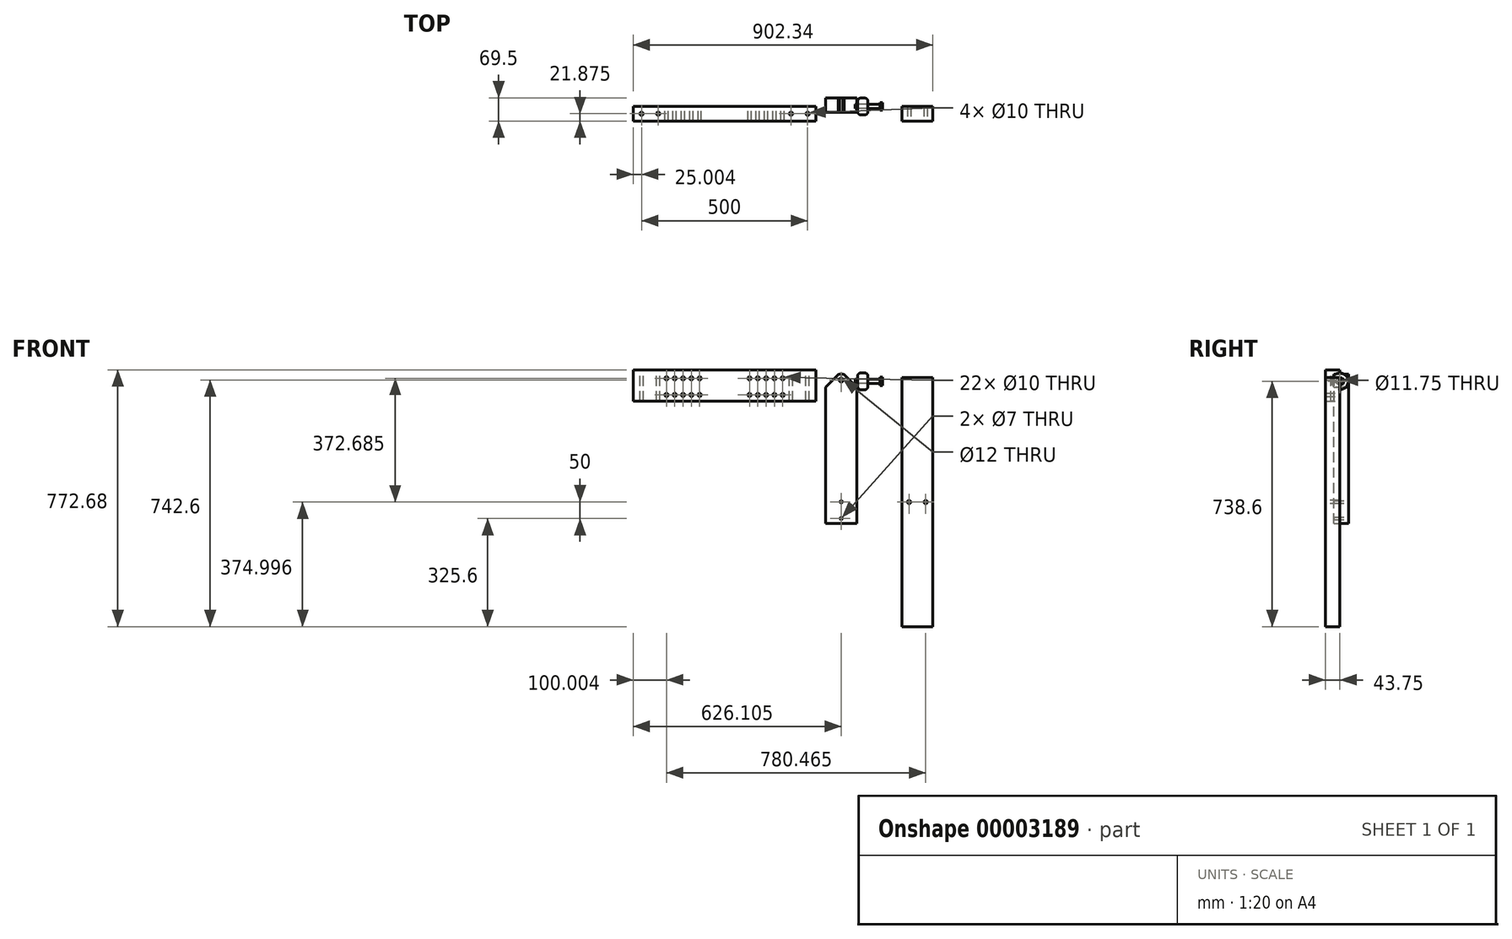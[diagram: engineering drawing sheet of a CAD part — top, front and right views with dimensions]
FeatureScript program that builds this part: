
annotation { "Feature Type Name" : "Feature", "Feature Type Description" : "" }
export const myFeature = defineFeature(function(context is Context, id is Id, definition is map)
    precondition{}
    {
        {
            var Q0;
            Q0=qCreatedBy(makeId("Top.planeOp"),FACE);
            var sketch = newSketch(context, id + "F0", { "sketchPlane" : qUnion([Q0])});
            skLineSegment(sketch, "E0.top", {"start": v(-30, 5.88) * mm, "end": v(0, 5.88) * mm});
            skLineSegment(sketch, "E0.left", {"start": v(-30, 17) * mm, "end": v(-30, 5.88) * mm});
            skLineSegment(sketch, "E0.right", {"start": v(0, 17) * mm, "end": v(0, 5.88) * mm});
            skLineSegment(sketch, "E1", {"start": v(0, 0) * mm, "end": v(-31.96, 0) * mm, "construction": true});
            skLineSegment(sketch, "E2", {"start": v(-22, 25) * mm, "end": v(-8, 25) * mm});
            skPoint(sketch, "E3.visualSharp", {"position": v(-30, 25) * mm});
            skArc(sketch, "E3.filletArc", {"start": v(-22, 25) * mm, "mid": v(-27.66, 22.66) * mm, "end": v(-30, 17) * mm});
            skPoint(sketch, "E4.visualSharp", {"position": v(0, 25) * mm});
            skArc(sketch, "E4.filletArc", {"start": v(0, 17) * mm, "mid": v(-2.34, 22.66) * mm, "end": v(-8, 25) * mm});
            skSolve(sketch);
        }
        {
            var Q0;
            Q0 = qSketchRegion(id + "F0", true);
            var Q1;
            Q1=sQuery(id+"F0.wireOp",EDGE,"E1");
            revolve(context, id + "F1", {"entities" : qUnion([Q0]), "axis" : qUnion([Q1]), "revolveType" : RevolveType.FULL});
        }
        {
            var Q0;
            Q0=qCreatedBy(makeId("Right.planeOp"),FACE);
            var sketch = newSketch(context, id + "F2", { "sketchPlane" : qUnion([Q0])});
            skCircle(sketch, "E5.0", {"center": v(0, 0) * mm, "radius": 5.88 * mm});
            skSolve(sketch);
        }
        {
            var Q0;
            Q0=makeQuery(id+"F2.imprint","IMPRINT",FACE,{"disambiguationData":[TD([[makeQuery(id+"F2.imprint","IMPRINT",EDGE,{"derivedFrom":sQuery(id+"F2.wireOp",EDGE,"E5.0")}),1.0]])]});
            extrude(context, id + "F3", {"entities" : qUnion([Q0]), "endBound" : BoundingType.SYMMETRIC, "depth" : (3 * 25) * mm});
        }
        {
            var Q0;
            Q0=makeQuery(id+"F3.opExtrude","CAP_FACE",FACE,{"disambiguationData":[OSD([sQuery(id+"F2.wireOp",EDGE,"E5.0")])],"isStart":false});
            var sketch = newSketch(context, id + "F4", { "sketchPlane" : qUnion([Q0])});
            skCircle(sketch, "E6.cCircle", {"center": v(0, 0) * mm, "radius": 10.81 * mm, "construction": true});
            skLineSegment(sketch, "E6.0", {"start": v(11.76, 4.21) * mm, "end": v(9.52, -8.08) * mm});
            skLineSegment(sketch, "E6.1", {"start": v(9.52, -8.08) * mm, "end": v(-2.23, -12.29) * mm});
            skLineSegment(sketch, "E6.2", {"start": v(-2.23, -12.29) * mm, "end": v(-11.76, -4.21) * mm});
            skLineSegment(sketch, "E6.3", {"start": v(-11.76, -4.21) * mm, "end": v(-9.52, 8.08) * mm});
            skLineSegment(sketch, "E6.4", {"start": v(-9.52, 8.08) * mm, "end": v(2.23, 12.29) * mm});
            skLineSegment(sketch, "E6.5", {"start": v(2.23, 12.29) * mm, "end": v(11.76, 4.21) * mm});
            skPoint(sketch, "E6.0.midPoint", {"position": v(10.64, -1.93) * mm});
            skSolve(sketch);
        }
        {
            var Q0;
            Q0=makeQuery(id+"F4.imprint","IMPRINT",FACE,{"disambiguationData":[TD([[makeQuery(id+"F4.imprint","IMPRINT",EDGE,{"derivedFrom":sQuery(id+"F4.wireOp",EDGE,"E6.0")}),-1.0]])]});
            var Q1;
            Q1=makeQuery(id+"F4.imprint","IMPRINT",FACE,{"disambiguationData":[TD([[makeQuery(id+"F4.imprint","IMPRINT",EDGE,{"derivedFrom":makeQuery(id+"F3.opExtrude","CAP_EDGE",EDGE,{"disambiguationData":[OSD([sQuery(id+"F2.wireOp",EDGE,"E5.0")])],"isStart":false})}),1.0]])]});
            extrude(context, id + "F5", {"entities" : qUnion([Q0, Q1]), "operationType" : NewBodyOperationType.ADD, "depth" : 7.7 * mm});
        }
        {
            var Q0;
            Q0=qCreatedBy(makeId("Front.planeOp"),FACE);
            var sketch = newSketch(context, id + "F6", { "sketchPlane" : qUnion([Q0])});
            skLineSegment(sketch, "E7.bottom", {"start": v(-155.98, 34.08) * mm, "end": v(-705.98, 34.08) * mm});
            skLineSegment(sketch, "E7.top", {"start": v(-155.98, -59.67) * mm, "end": v(-705.98, -59.67) * mm});
            skLineSegment(sketch, "E7.left", {"start": v(-155.98, 34.08) * mm, "end": v(-155.98, -59.67) * mm});
            skLineSegment(sketch, "E7.right", {"start": v(-705.98, 34.08) * mm, "end": v(-705.98, -59.67) * mm});
            skLineSegment(sketch, "E8", {"start": v(-430.98, 34.08) * mm, "end": v(-430.98, -337.68) * mm, "construction": true});
            skCircle(sketch, "E9", {"center": v(-605.98, 9.08) * mm, "radius": 5 * mm});
            skCircle(sketch, "E10", {"center": v(-580.98, 9.08) * mm, "radius": 5 * mm});
            skCircle(sketch, "E11", {"center": v(-555.98, 9.08) * mm, "radius": 5 * mm});
            skCircle(sketch, "E12", {"center": v(-530.98, 9.08) * mm, "radius": 5 * mm});
            skCircle(sketch, "E13", {"center": v(-505.98, 9.08) * mm, "radius": 5 * mm});
            skCircle(sketch, "E14", {"center": v(-605.98, -40.92) * mm, "radius": 5 * mm});
            skCircle(sketch, "E15", {"center": v(-580.98, -40.92) * mm, "radius": 5 * mm});
            skCircle(sketch, "E16", {"center": v(-555.98, -40.92) * mm, "radius": 5 * mm});
            skCircle(sketch, "E17", {"center": v(-530.98, -40.92) * mm, "radius": 5 * mm});
            skCircle(sketch, "E18", {"center": v(-505.98, -40.92) * mm, "radius": 5 * mm});
            skLineSegment(sketch, "E19", {"start": v(-605.98, 9.08) * mm, "end": v(-580.98, 9.08) * mm, "construction": true});
            skLineSegment(sketch, "E20", {"start": v(-555.98, 9.08) * mm, "end": v(-580.98, 9.08) * mm, "construction": true});
            skLineSegment(sketch, "E21", {"start": v(-555.98, 9.08) * mm, "end": v(-530.98, 9.08) * mm, "construction": true});
            skLineSegment(sketch, "E22", {"start": v(-530.98, 9.08) * mm, "end": v(-505.98, 9.08) * mm, "construction": true});
            skLineSegment(sketch, "E23", {"start": v(-505.98, -40.92) * mm, "end": v(-530.98, -40.92) * mm, "construction": true});
            skLineSegment(sketch, "E24", {"start": v(-555.98, -40.92) * mm, "end": v(-530.98, -40.92) * mm, "construction": true});
            skLineSegment(sketch, "E25", {"start": v(-555.98, -40.92) * mm, "end": v(-580.98, -40.92) * mm, "construction": true});
            skLineSegment(sketch, "E26", {"start": v(-580.98, -40.92) * mm, "end": v(-605.98, -40.92) * mm, "construction": true});
            skLineSegment(sketch, "E27", {"start": v(-605.98, 9.08) * mm, "end": v(-605.98, -40.92) * mm, "construction": true});
            skLineSegment(sketch, "E28.0.MirrorCS", {"start": v(-305.98, 9.08) * mm, "end": v(-330.98, 9.08) * mm, "construction": true});
            skLineSegment(sketch, "E28.1.MirrorCS", {"start": v(-305.98, -40.92) * mm, "end": v(-330.98, -40.92) * mm, "construction": true});
            skLineSegment(sketch, "E28.2.MirrorCS", {"start": v(-255.98, 9.08) * mm, "end": v(-255.98, -40.92) * mm, "construction": true});
            skCircle(sketch, "E28.3.MirrorC", {"center": v(-255.98, -40.92) * mm, "radius": 5 * mm});
            skCircle(sketch, "E28.4.MirrorC", {"center": v(-305.98, 9.08) * mm, "radius": 5 * mm});
            skCircle(sketch, "E28.5.MirrorC", {"center": v(-255.98, 9.08) * mm, "radius": 5 * mm});
            skLineSegment(sketch, "E28.6.MirrorCS", {"start": v(-280.98, -40.92) * mm, "end": v(-255.98, -40.92) * mm, "construction": true});
            skLineSegment(sketch, "E28.7.MirrorCS", {"start": v(-255.98, 9.08) * mm, "end": v(-280.98, 9.08) * mm, "construction": true});
            skCircle(sketch, "E28.8.MirrorC", {"center": v(-330.98, -40.92) * mm, "radius": 5 * mm});
            skLineSegment(sketch, "E28.9.MirrorCS", {"start": v(-305.98, -40.92) * mm, "end": v(-280.98, -40.92) * mm, "construction": true});
            skLineSegment(sketch, "E28.10.MirrorCS", {"start": v(-305.98, 9.08) * mm, "end": v(-280.98, 9.08) * mm, "construction": true});
            skCircle(sketch, "E28.11.MirrorC", {"center": v(-330.98, 9.08) * mm, "radius": 5 * mm});
            skLineSegment(sketch, "E28.12.MirrorCS", {"start": v(-355.98, -40.92) * mm, "end": v(-330.98, -40.92) * mm, "construction": true});
            skCircle(sketch, "E28.13.MirrorC", {"center": v(-355.98, 9.08) * mm, "radius": 5 * mm});
            skCircle(sketch, "E28.14.MirrorC", {"center": v(-280.98, -40.92) * mm, "radius": 5 * mm});
            skLineSegment(sketch, "E28.15.MirrorCS", {"start": v(-330.98, 9.08) * mm, "end": v(-355.98, 9.08) * mm, "construction": true});
            skCircle(sketch, "E28.16.MirrorC", {"center": v(-280.98, 9.08) * mm, "radius": 5 * mm});
            skCircle(sketch, "E28.17.MirrorC", {"center": v(-355.98, -40.92) * mm, "radius": 5 * mm});
            skCircle(sketch, "E28.18.MirrorC", {"center": v(-305.98, -40.92) * mm, "radius": 5 * mm});
            skSolve(sketch);
        }
        {
            var Q0;
            Q0=makeQuery(id+"F6.imprint","IMPRINT",FACE,{"disambiguationData":[TD([[makeQuery(id+"F6.imprint","IMPRINT",EDGE,{"derivedFrom":sQuery(id+"F6.wireOp",EDGE,"E7.bottom")}),1.0]])]});
            extrude(context, id + "F7", {"entities" : qUnion([Q0]), "depth" : (1.75 * 25) * mm});
        }
        {
            var Q0;
            Q0=makeQuery(id+"F7.opExtrude","SWEPT_FACE",FACE,{"disambiguationData":[OSD([sQuery(id+"F6.wireOp",EDGE,"E7.bottom")])]});
            var sketch = newSketch(context, id + "F8", { "sketchPlane" : qUnion([Q0])});
            skCircle(sketch, "E29", {"center": v(-180.98, -21.88) * mm, "radius": 5 * mm});
            skCircle(sketch, "E30", {"center": v(-230.98, -21.88) * mm, "radius": 5 * mm});
            skLineSegment(sketch, "E31", {"start": v(-230.98, -21.88) * mm, "end": v(-180.98, -21.88) * mm, "construction": true});
            skLineSegment(sketch, "E32", {"start": v(-155.98, -21.88) * mm, "end": v(-93.47, -21.88) * mm, "construction": true});
            skLineSegment(sketch, "E33", {"start": v(-430.98, 0) * mm, "end": v(-430.98, -256.46) * mm, "construction": true});
            skLineSegment(sketch, "E34.0.MirrorCS", {"start": v(-630.98, -21.88) * mm, "end": v(-680.98, -21.88) * mm, "construction": true});
            skCircle(sketch, "E35.0.MirrorC", {"center": v(-630.98, -21.88) * mm, "radius": 5 * mm});
            skCircle(sketch, "E36.0.MirrorC", {"center": v(-680.98, -21.88) * mm, "radius": 5 * mm});
            skSolve(sketch);
        }
        {
            var Q0;
            Q0 = qSketchRegion(id + "F8", true);
            extrude(context, id + "F9", {"entities" : qUnion([Q0]), "operationType" : NewBodyOperationType.REMOVE, "endBound" : BoundingType.THROUGH_ALL, "oppositeDirection" : true, "depth" : 25 * mm});
        }
        {
            var Q0;
            Q0=qCreatedBy(makeId("Right.planeOp"),FACE);
            cPlane(context, id + "F10", {"entities" : qUnion([Q0]), "cplaneType" : CPlaneType.OFFSET, "offset" : 33 * mm, "oppositeDirection" : true, "width" : 150 * mm, "height" : 150 * mm});
        }
        {
            var Q0;
            Q0=qCreatedBy(id+"F10.planeOp",FACE);
            var sketch = newSketch(context, id + "F11", { "sketchPlane" : qUnion([Q0])});
            skLineSegment(sketch, "E37.bottom", {"start": v(-18, -428) * mm, "end": v(25.75, -428) * mm});
            skLineSegment(sketch, "E37.top", {"start": v(-18, 22) * mm, "end": v(25.75, 22) * mm});
            skLineSegment(sketch, "E37.left", {"start": v(-18, -428) * mm, "end": v(-18, 22) * mm});
            skLineSegment(sketch, "E37.right", {"start": v(25.75, -428) * mm, "end": v(25.75, 22) * mm});
            skSolve(sketch);
        }
        {
            var Q0;
            Q0=makeQuery(id+"F11.imprint","IMPRINT",FACE,{"disambiguationData":[TD([[makeQuery(id+"F11.imprint","IMPRINT",EDGE,{"derivedFrom":sQuery(id+"F11.wireOp",EDGE,"E37.bottom")}),1.0]])]});
            extrude(context, id + "F12", {"entities" : qUnion([Q0]), "oppositeDirection" : true, "depth" : (3.75 * 25) * mm});
        }
        {
            var Q0;
            Q0=makeQuery(id+"F12.opExtrude","SWEPT_FACE",FACE,{"disambiguationData":[OSD([sQuery(id+"F11.wireOp",EDGE,"E37.right")])]});
            var sketch = newSketch(context, id + "F13", { "sketchPlane" : qUnion([Q0])});
            skCircle(sketch, "E38", {"center": v(79.88, -363) * mm, "radius": 3.5 * mm});
            skCircle(sketch, "E39", {"center": v(79.88, -413) * mm, "radius": 3.5 * mm});
            skLineSegment(sketch, "E40", {"start": v(79.88, -413) * mm, "end": v(79.88, -363) * mm, "construction": true});
            skLineSegment(sketch, "E41", {"start": v(79.88, -428) * mm, "end": v(79.88, 34.96) * mm, "construction": true});
            skCircle(sketch, "E42", {"center": v(79.88, 4) * mm, "radius": 6 * mm});
            skSolve(sketch);
        }
        {
            var Q0;
            Q0 = qSketchRegion(id + "F13", true);
            extrude(context, id + "F14", {"entities" : qUnion([Q0]), "operationType" : NewBodyOperationType.REMOVE, "endBound" : BoundingType.THROUGH_ALL, "oppositeDirection" : true, "depth" : 25 * mm});
        }
        {
            var Q0;
            Q0=makeQuery(id+"F12.opExtrude","CAP_EDGE",EDGE,{"disambiguationData":[OSD([sQuery(id+"F11.wireOp",EDGE,"E37.top")])],"isStart":false});
            var Q1;
            Q1=makeQuery(id+"F12.opExtrude","CAP_EDGE",EDGE,{"disambiguationData":[OSD([sQuery(id+"F11.wireOp",EDGE,"E37.top")])],"isStart":true});
            chamfer(context, id + "F15", {"entities" : qUnion([Q0, Q1]), "width" : 40 * mm, "tangentPropagation" : true});
        }
        {
            var Q0;
            {var subQ0=sQuery(id+"F11.wireOp",EDGE,"E37.top");Q0=makeQuery(id+"F15.opChamfer","BLEND_EDGE",EDGE,{"blendedFrom":[makeQuery(id+"F12.opExtrude","CAP_EDGE",EDGE,{"disambiguationData":[OSD([subQ0])],"isStart":false}),makeQuery(id+"F12.opExtrude","SWEPT_FACE",FACE,{"disambiguationData":[OSD([subQ0])]})],"blendedInto":[makeQuery(id+"F12.opExtrude","SWEPT_FACE",FACE,{"disambiguationData":[OSD([subQ0])]})]});}
            var Q1;
            {var subQ0=sQuery(id+"F11.wireOp",EDGE,"E37.top");Q1=makeQuery(id+"F15.opChamfer","BLEND_EDGE",EDGE,{"blendedFrom":[makeQuery(id+"F12.opExtrude","CAP_EDGE",EDGE,{"disambiguationData":[OSD([subQ0])],"isStart":true}),makeQuery(id+"F12.opExtrude","SWEPT_FACE",FACE,{"disambiguationData":[OSD([subQ0])]})],"blendedInto":[makeQuery(id+"F12.opExtrude","SWEPT_FACE",FACE,{"disambiguationData":[OSD([subQ0])]})]});}
            chamfer(context, id + "F16", {"entities" : qUnion([Q0, Q1]), "width" : 5 * mm, "tangentPropagation" : true});
        }
        {
            var Q0;
            Q0=qCreatedBy(makeId("Front.planeOp"),FACE);
            var sketch = newSketch(context, id + "F17", { "sketchPlane" : qUnion([Q0])});
            skLineSegment(sketch, "E43.bottom", {"start": v(196.36, 11.4) * mm, "end": v(102.61, 11.4) * mm});
            skLineSegment(sketch, "E43.top", {"start": v(196.36, -738.6) * mm, "end": v(102.61, -738.6) * mm});
            skLineSegment(sketch, "E43.left", {"start": v(196.36, 11.4) * mm, "end": v(196.36, -738.6) * mm});
            skLineSegment(sketch, "E43.right", {"start": v(102.61, 11.4) * mm, "end": v(102.61, -738.6) * mm});
            skSolve(sketch);
        }
        {
            var Q0;
            Q0=makeQuery(id+"F17.imprint","IMPRINT",FACE,{"disambiguationData":[TD([[makeQuery(id+"F17.imprint","IMPRINT",EDGE,{"derivedFrom":sQuery(id+"F17.wireOp",EDGE,"E43.bottom")}),1.0]])]});
            extrude(context, id + "F18", {"entities" : qUnion([Q0]), "depth" : (25 * 1.75) * mm});
        }
        {
            var Q0;
            Q0=makeQuery(id+"F18.opExtrude","CAP_FACE",FACE,{"disambiguationData":[OSD([sQuery(id+"F17.wireOp",EDGE,"E43.bottom"),sQuery(id+"F17.wireOp",EDGE,"E43.top"),sQuery(id+"F17.wireOp",EDGE,"E43.left"),sQuery(id+"F17.wireOp",EDGE,"E43.right")])],"isStart":false});
            var sketch = newSketch(context, id + "F19", { "sketchPlane" : qUnion([Q0])});
            skCircle(sketch, "E44", {"center": v(174.49, -363.6) * mm, "radius": 5 * mm});
            skCircle(sketch, "E45", {"center": v(124.49, -363.6) * mm, "radius": 5 * mm});
            skLineSegment(sketch, "E46", {"start": v(274.4, -363.6) * mm, "end": v(196.36, -363.6) * mm, "construction": true});
            skLineSegment(sketch, "E47", {"start": v(149.49, 11.4) * mm, "end": v(149.49, -809.63) * mm});
            skLineSegment(sketch, "E48", {"start": v(124.49, -363.6) * mm, "end": v(149.49, -363.6) * mm, "construction": true});
            skLineSegment(sketch, "E49", {"start": v(149.49, -363.6) * mm, "end": v(174.49, -363.6) * mm, "construction": true});
            skSolve(sketch);
        }
        {
            var Q0;
            Q0 = qSketchRegion(id + "F19", true);
            extrude(context, id + "F20", {"entities" : qUnion([Q0]), "operationType" : NewBodyOperationType.REMOVE, "endBound" : BoundingType.THROUGH_ALL, "oppositeDirection" : true, "depth" : 25 * mm});
        }
    });
